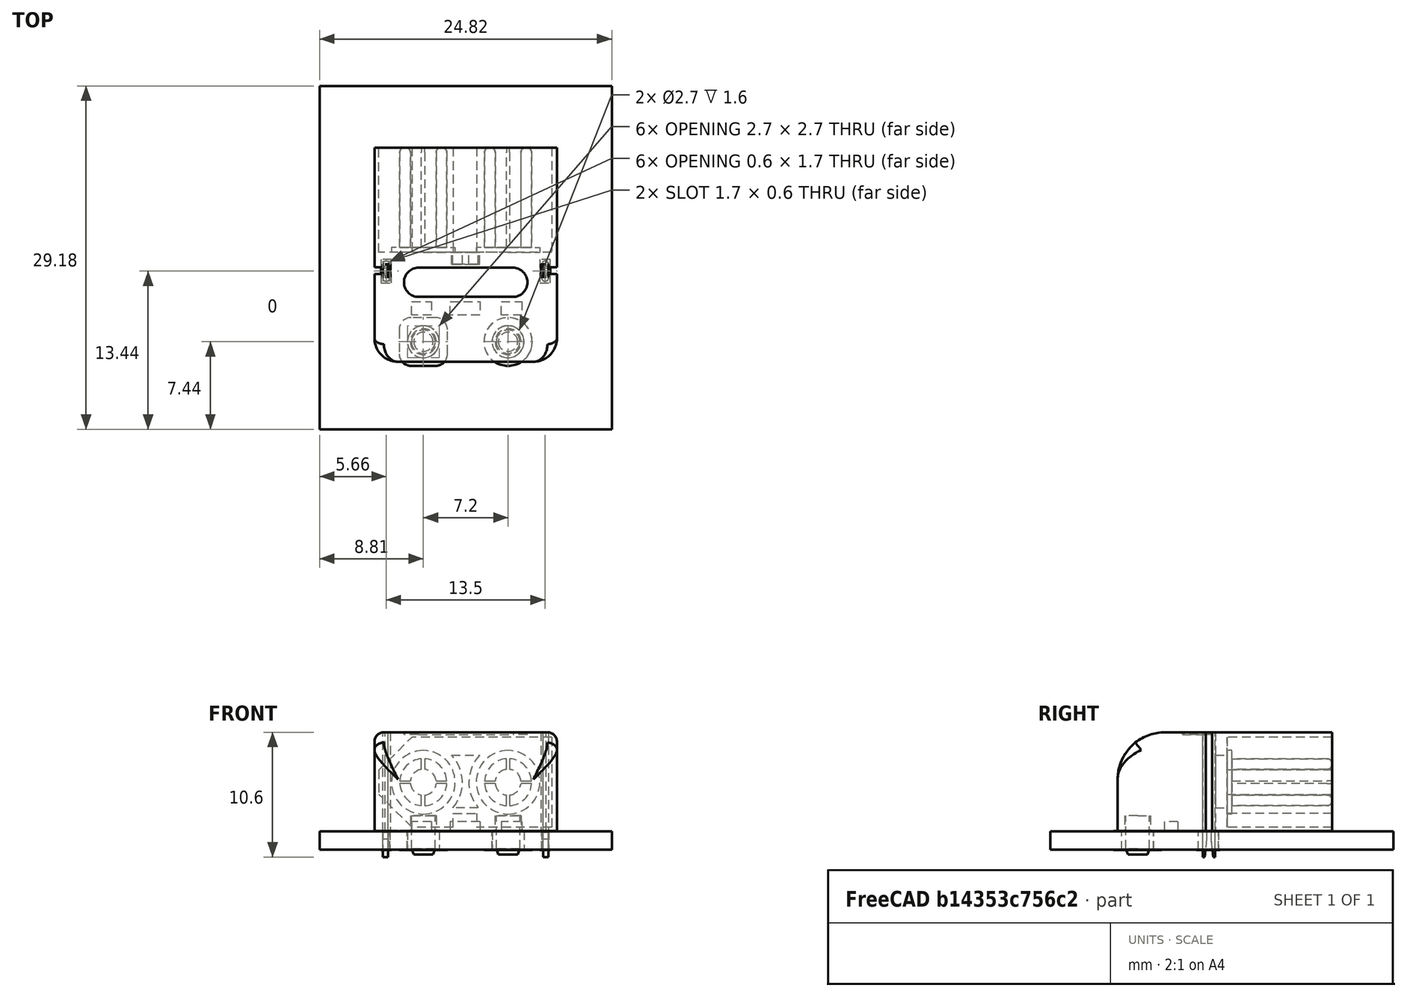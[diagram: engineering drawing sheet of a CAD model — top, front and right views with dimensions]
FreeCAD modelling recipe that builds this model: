
FCSTD DOCUMENT  (FreeCAD 1.0R39285 (Git))
Label: XT60PW-M
License: All rights reserved
LicenseURL: https://en.wikipedia.org/wiki/All_rights_reserved
objects: Part::Feature×11, Sketcher::SketchObject×3, Part::Compound×1, App::DocumentObjectGroup×1
note: 18 computed .brp shape members not serialized (recipe doc carries the construction recipe); baked Part::Feature solids carry a one-line shape summary decoded from their .brp

FEATURE [Part::Feature] anr_  label="drill_000"
  shape: bbox 0.6199 x 1.72 x 1.6 mm, 10 faces (baked)
FEATURE [Part::Feature] anr_001  label="drill_001"
  shape: bbox 0.6199 x 1.72 x 1.6 mm, 10 faces (baked)
FEATURE [Part::Feature] anr_002  label="drill_002"
  shape: bbox 2.72 x 2.72 x 1.6 mm, 4 faces (baked)
FEATURE [Part::Feature] anr_003  label="drill_003"
  shape: bbox 2.72 x 2.72 x 1.6 mm, 4 faces (baked)
FEATURE [Part::Compound] annulars  label="TH-Drills"
  Links = -> [anr_,anr_001,anr_002,anr_003]
FEATURE [Part::Feature] Shape001  label="topPads"
  Placement = pos=(0,0,-0.01) rot=(0,0,1;0rad)
  shape: bbox 14.4 x 9.05 x 0.01 mm, 39 faces, 4 solids (baked)
FEATURE [Part::Feature] Shape002  label="btmPads"
  Placement = pos=(0,0,-1.6) rot=(0,0,1;0rad)
  shape: bbox 14.4 x 9.05 x 0.01 mm, 39 faces, 4 solids (baked)
FEATURE [Part::Feature] Shape  label="F.SilkS_outline_"
  Placement = pos=(0,0,0.01) rot=(0,0,1;0rad)
  shape: bbox 15.84 x 18.54 x 2e-07 mm, 0 faces, 0 solids (baked)
FEATURE [Sketcher::SketchObject] _F_SilkS__sketch  label="F.SilkS_"
  ArcFitTolerance = 1e-06
  FullyConstrained = false
  MakeInternals = false
  Placement = pos=(0,0,0.01) rot=(0,0,1;0rad)
  sketch-geometry (6):
    g0: LineSegment StartX=-4.26 StartY=16.46 StartZ=0 EndX=-4.26 EndY=2.15 EndZ=0
    g1: LineSegment StartX=-4.26 StartY=16.46 StartZ=0 EndX=11.46 EndY=16.46 EndZ=0
    g2: LineSegment StartX=2.31 StartY=-1.96 StartZ=0 EndX=6.05 EndY=-1.96 EndZ=0
    g3: LineSegment StartX=11.46 StartY=16.46 StartZ=0 EndX=11.46 EndY=2.15 EndZ=0
    g4: ArcOfCircle CenterX=-0.150001 CenterY=2.15 CenterZ=0 NormalX=0 NormalY=0 NormalZ=1 AngleXU=-2.11185 Radius=4.11 StartAngle=5.25344 EndAngle=6.28319
    g5: ArcOfCircle CenterX=7.35 CenterY=2.15 CenterZ=0 NormalX=0 NormalY=0 NormalZ=1 AngleXU=2.25539e-07 Radius=4.11 StartAngle=5.00909 EndAngle=6.28319
FEATURE [Part::Feature] Shape003  label="F.CrtYd_outline_"
  Placement = pos=(0,0,0.01) rot=(0,0,1;0rad)
  shape: bbox 16.55 x 19.45 x 2e-07 mm, 0 faces, 0 solids (baked)
FEATURE [Sketcher::SketchObject] _F_CrtYd__sketch  label="F.CrtYd_"
  ArcFitTolerance = 1e-06
  FullyConstrained = false
  MakeInternals = false
  Placement = pos=(0,0,0.01) rot=(0,0,1;0rad)
  sketch-geometry (4):
    g0: LineSegment StartX=-4.65 StartY=16.85 StartZ=0 EndX=-4.65 EndY=-2.55 EndZ=0
    g1: LineSegment StartX=-4.65 StartY=16.85 StartZ=0 EndX=11.85 EndY=16.85 EndZ=0
    g2: LineSegment StartX=11.85 StartY=16.85 StartZ=0 EndX=11.85 EndY=-2.55 EndZ=0
    g3: LineSegment StartX=11.85 StartY=-2.55 StartZ=0 EndX=-4.65 EndY=-2.55 EndZ=0
FEATURE [Part::Feature] Shape004  label="F.Fab_outline_"
  Placement = pos=(0,0,0.01) rot=(0,0,1;0rad)
  shape: bbox 15.6 x 18.3 x 2e-07 mm, 0 faces, 0 solids (baked)
FEATURE [Sketcher::SketchObject] _F_Fab__sketch  label="F.Fab_"
  ArcFitTolerance = 1e-06
  FullyConstrained = false
  MakeInternals = false
  Placement = pos=(0,0,0.01) rot=(0,0,1;0rad)
  sketch-geometry (6):
    g0: LineSegment StartX=-4.15 StartY=16.35 StartZ=0 EndX=-4.15 EndY=2.15 EndZ=0
    g1: LineSegment StartX=-4.15 StartY=16.35 StartZ=0 EndX=11.35 EndY=16.35 EndZ=0
    g2: LineSegment StartX=-0.15 StartY=-1.85 StartZ=0 EndX=7.35 EndY=-1.85 EndZ=0
    g3: LineSegment StartX=11.35 StartY=16.35 StartZ=0 EndX=11.35 EndY=2.15 EndZ=0
    g4: ArcOfCircle CenterX=-0.15 CenterY=2.15 CenterZ=0 NormalX=0 NormalY=0 NormalZ=1 AngleXU=-1.5708 Radius=4 StartAngle=4.71239 EndAngle=6.28319
    g5: ArcOfCircle CenterX=7.35 CenterY=2.15 CenterZ=0 NormalX=0 NormalY=0 NormalZ=1 AngleXU=-1.06478e-07 Radius=4 StartAngle=4.71239 EndAngle=6.28319
FEATURE [Part::Feature] PCB
  shape: bbox 24.83 x 29.18 x 1.58 mm, 20 faces (baked)
FEATURE [App::DocumentObjectGroup] Group  label="AMASS_XT60PW-M_1x02_P7.20mm_Horizontal-fp"
  Group = -> [Shape001,Shape002,annulars,_F_SilkS__sketch,Shape,_F_CrtYd__sketch,Shape003,_F_Fab__sketch,Shape004,PCB]
FEATURE [Part::Feature] Shape190  label="XT60PW-M"
  shape: bbox 15.5 x 18.2 x 10.93 mm, 174 faces (baked)
